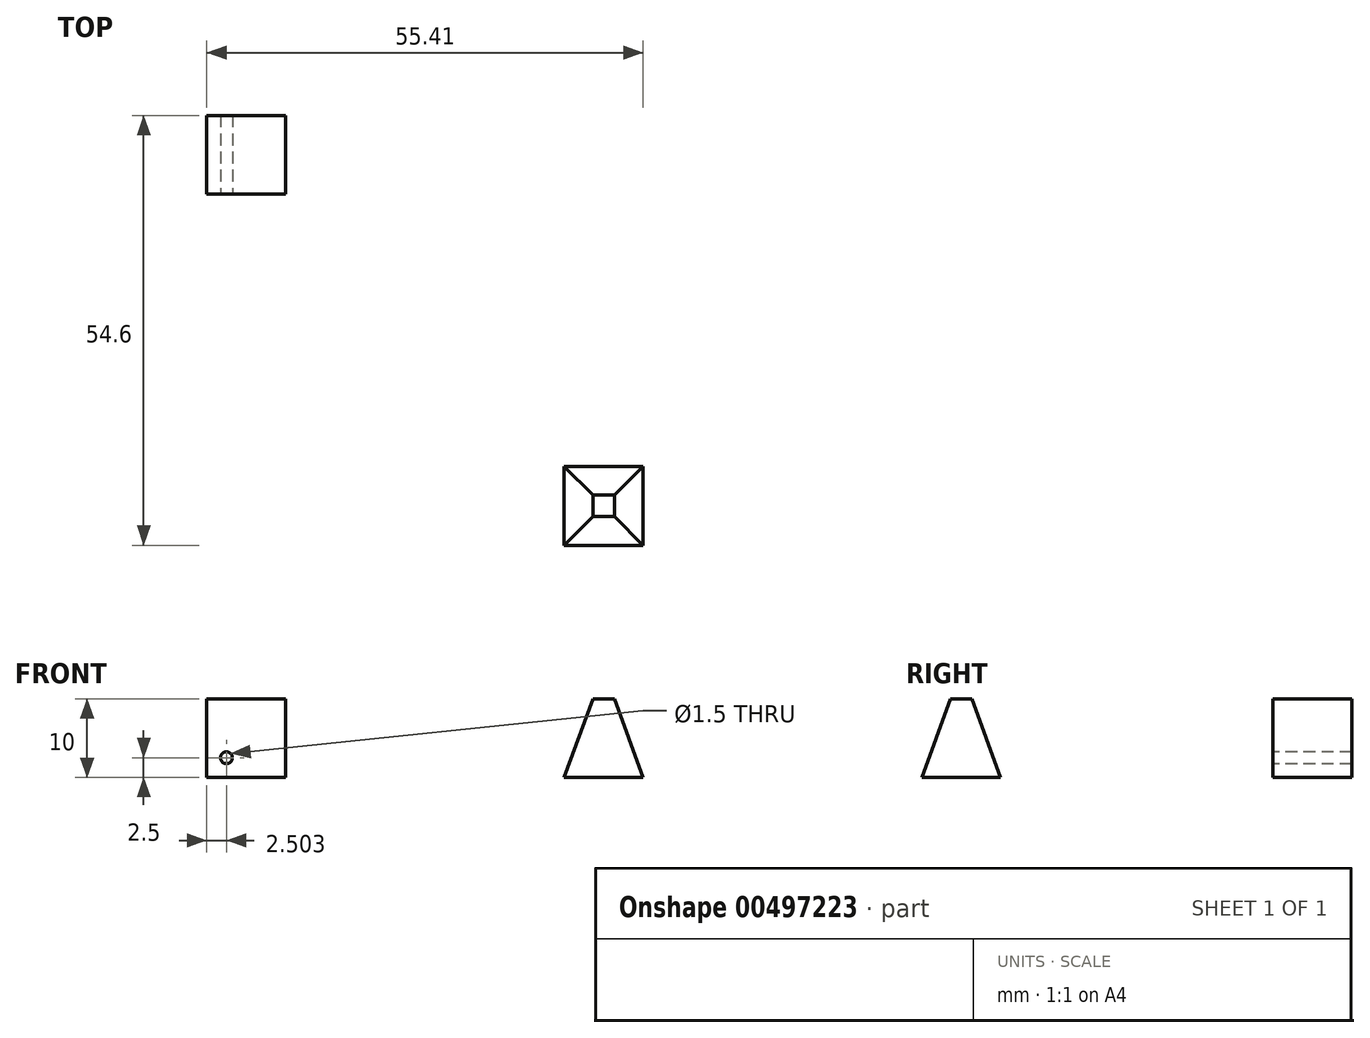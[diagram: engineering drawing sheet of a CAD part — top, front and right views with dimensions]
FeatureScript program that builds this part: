
annotation { "Feature Type Name" : "Feature", "Feature Type Description" : "" }
export const myFeature = defineFeature(function(context is Context, id is Id, definition is map)
    precondition{}
    {
        {
            var Q0;
            Q0=qCreatedBy(makeId("Top.planeOp"),FACE);
            var sketch = newSketch(context, id + "F0", { "sketchPlane" : qUnion([Q0])});
            skLineSegment(sketch, "E0.bottom", {"start": v(-29.66, 0) * mm, "end": v(-19.66, 0) * mm});
            skLineSegment(sketch, "E0.top", {"start": v(-29.66, 10) * mm, "end": v(-19.66, 10) * mm});
            skLineSegment(sketch, "E0.left", {"start": v(-29.66, 0) * mm, "end": v(-29.66, 10) * mm});
            skLineSegment(sketch, "E0.right", {"start": v(-19.66, 0) * mm, "end": v(-19.66, 10) * mm});
            skSolve(sketch);
        }
        {
            var Q0;
            Q0 = qSketchRegion(id + "F0", true);
            extrude(context, id + "F1", {"entities" : qUnion([Q0]), "depth" : 10 * mm});
        }
        {
            var Q0;
            Q0=qCreatedBy(makeId("Top.planeOp"),FACE);
            var sketch = newSketch(context, id + "F2", { "sketchPlane" : qUnion([Q0])});
            skLineSegment(sketch, "E1.bottom", {"start": v(15.75, -34.6) * mm, "end": v(25.75, -34.6) * mm});
            skLineSegment(sketch, "E1.top", {"start": v(15.75, -44.6) * mm, "end": v(25.75, -44.6) * mm});
            skLineSegment(sketch, "E1.left", {"start": v(15.75, -34.6) * mm, "end": v(15.75, -44.6) * mm});
            skLineSegment(sketch, "E1.right", {"start": v(25.75, -34.6) * mm, "end": v(25.75, -44.6) * mm});
            skSolve(sketch);
        }
        {
            var Q0;
            Q0 = qSketchRegion(id + "F2", true);
            extrude(context, id + "F3", {"entities" : qUnion([Q0]), "depth" : 10 * mm, "hasDraft" : true, "draftAngle" : 20 * degree, "draftPullDirection" : true});
        }
        {
            var Q0;
            Q0=makeQuery(id+"F1.opExtrude","SWEPT_FACE",FACE,{"disambiguationData":[OSD([sQuery(id+"F0.wireOp",EDGE,"E0.bottom")])]});
            var sketch = newSketch(context, id + "F4", { "sketchPlane" : qUnion([Q0])});
            skCircle(sketch, "E2", {"center": v(-27.16, 2.5) * mm, "radius": 0.75 * mm});
            skSolve(sketch);
        }
        {
            var Q0;
            Q0 = qSketchRegion(id + "F4", true);
            extrude(context, id + "F5", {"entities" : qUnion([Q0]), "operationType" : NewBodyOperationType.REMOVE, "oppositeDirection" : true, "depth" : 25 * mm});
        }
    });
